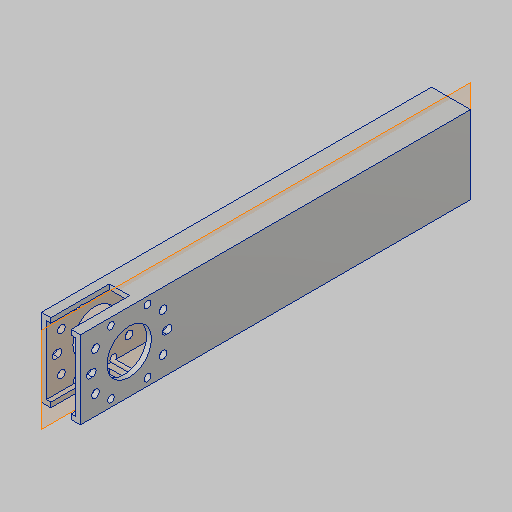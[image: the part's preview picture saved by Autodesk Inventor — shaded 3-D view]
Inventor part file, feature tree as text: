
AUTODESK INVENTOR PART (.ipt)
format: ipt  version: 2023.5 (Build 275446000, 446)  size: 176,640 bytes
history: native  units: in
note: dims shown in document units (in); Inventor stores cm internally (conversion verified against a paired STEP export)
features: hole x3, extrude x2, sketch x2, projected_geometry x1
ambient origin geometry x8: Origin, YZ Plane, XZ Plane, XY Plane, X Axis, Y Axis, Z Axis, Center Point
bodies: Solid1 (feature_tree)
feature tree (8):
  extrude  "Extrusion1"  Depth=1.25in
  sketch  "Sketch2"  dims[d4=0.0in d5=1.25in]
  hole  "Hole1"  [1 undecoded]
  hole  "Hole2"  [1 undecoded]
  hole  "Hole3"  [1 undecoded]
  extrude  "Extrusion2"  Depth=1.0in TaperAngle=360.0deg
  sketch  "Sketch3"  dims[d6=1.14in d7=0.75in d8=0.375in d9=0.25in d10=0.5635in d11=1.0in d12=0.8108in d13=1.875in d14=2.0in d15=4.7244in d17=360.0deg d19=2.3622in d21=360.0deg d23=0.201in d24=0.75in d25=0.332in d26=0.25in d27=0.5635in d28=1.0in d29=0.8108in d30=0.177in d31=0.75in d32=0.385in d33=0.25in d34=0.5635in d35=1.0in d36=0.8108in d37=0.52in d38=1.5in d39=1.0in d40=0.0in]
  projected_geometry  "Project Cut Edges1"
note: 3 required parameter values undecoded (feature->parameter linkage not recoverable at this tier; creation-order binding heuristic only, values carry confidence <= 0.55)
